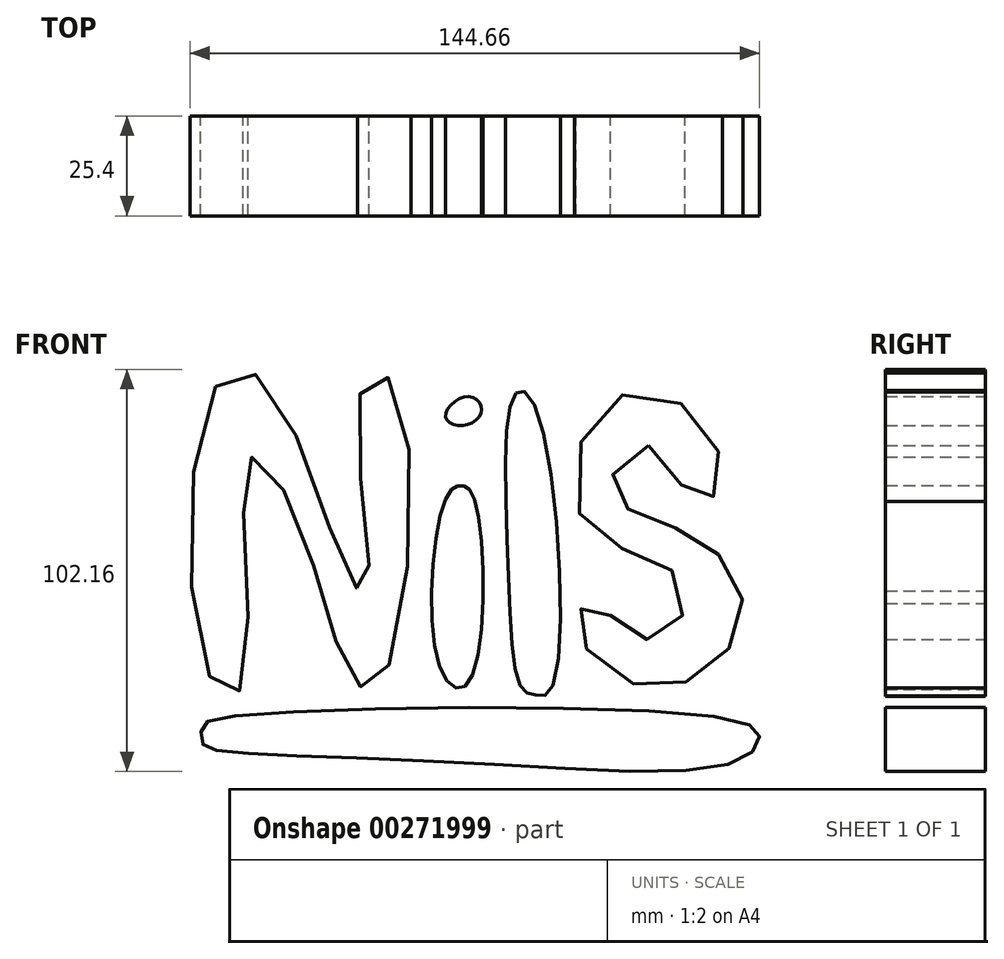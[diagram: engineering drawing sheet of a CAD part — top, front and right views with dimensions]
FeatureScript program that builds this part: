
annotation { "Feature Type Name" : "Feature", "Feature Type Description" : "" }
export const myFeature = defineFeature(function(context is Context, id is Id, definition is map)
    precondition{}
    {
        {
            var Q0;
            Q0=qCreatedBy(makeId("Front.planeOp"),FACE);
            var sketch = newSketch(context, id + "F0", { "sketchPlane" : qUnion([Q0])});
            skFitSpline(sketch, "E0", {"points": [v(-71.07, 25.18) * mm, v(-71.77, -50.12) * mm, v(-64.48, -51.3) * mm, v(-62.83, 6.35) * mm, v(-50.83, -7.3) * mm, v(-36, -49.42) * mm, v(-29.18, -49.89) * mm, v(-25.65, 25.41) * mm, v(-33.65, 25.65) * mm, v(-32.47, -25.18) * mm, v(-35.3, -26.12) * mm, v(-57.42, 24.94) * mm, v(-71.07, 25.18) * mm]});
            skFitSpline(sketch, "E1", {"points": [v(-70.8, -67.3) * mm, v(-9.62, -70.36) * mm, v(61.45, -70.13) * mm, v(67.1, -64) * mm, v(57.92, -59.07) * mm, v(-68.45, -58.83) * mm, v(-74.57, -61.65) * mm, v(-74.57, -65.42) * mm, v(-70.8, -67.3) * mm]});
            skSolve(sketch);
        }
        {
            var Q0;
            Q0=makeQuery(id+"F0.imprint","IMPRINT",FACE,{"disambiguationData":[TD([[makeQuery(id+"F0.imprint","IMPRINT",EDGE,{"derivedFrom":sQuery(id+"F0.wireOp",EDGE,"E0")}),1.0]])]});
            extrude(context, id + "F1", {"entities" : qUnion([Q0]), "depth" : 25.4 * mm});
        }
        {
            var Q0;
            Q0=qCreatedBy(makeId("Front.planeOp"),FACE);
            var sketch = newSketch(context, id + "F2", { "sketchPlane" : qUnion([Q0])});
            skFitSpline(sketch, "E2", {"points": [v(-12.68, -3.53) * mm, v(-13.62, -47.54) * mm, v(-7.03, -50.36) * mm, v(-5.15, -4) * mm, v(-8.68, 0) * mm, v(-12.68, -3.53) * mm]});
            skFitSpline(sketch, "E3", {"points": [v(-12.68, 17.41) * mm, v(-7.5, 15.3) * mm, v(-3.5, 19.53) * mm, v(-7.5, 22.6) * mm, v(-12.68, 17.41) * mm]});
            skFitSpline(sketch, "E4", {"points": [v(5.2, 23.53) * mm, v(3.08, -17.88) * mm, v(6.85, -51.77) * mm, v(10.14, -53.18) * mm, v(14.15, -52) * mm, v(10.38, 19.53) * mm, v(5.2, 23.53) * mm]});
            skFitSpline(sketch, "E5", {"points": [v(38.85, 10.12) * mm, v(50.62, -3.53) * mm, v(57.2, 0) * mm, v(48.97, 19.53) * mm, v(26.62, 19.53) * mm, v(23.32, -10.82) * mm, v(43.33, -20.24) * mm, v(47.1, -34.12) * mm, v(35.32, -38.6) * mm, v(25.68, -30.12) * mm, v(20.5, -34.12) * mm, v(32.5, -49.42) * mm, v(51.8, -48.24) * mm, v(62.86, -32.47) * mm, v(55.33, -16.24) * mm, v(38.62, -8.24) * mm, v(29.2, 0) * mm, v(38.85, 10.12) * mm]});
            skSolve(sketch);
        }
        {
            var Q0;
            Q0=makeQuery(id+"F2.imprint","IMPRINT",FACE,{"disambiguationData":[TD([[makeQuery(id+"F2.imprint","IMPRINT",EDGE,{"derivedFrom":sQuery(id+"F2.wireOp",EDGE,"E2")}),1.0]])]});
            var Q1;
            Q1=makeQuery(id+"F2.imprint","IMPRINT",FACE,{"disambiguationData":[TD([[makeQuery(id+"F2.imprint","IMPRINT",EDGE,{"derivedFrom":sQuery(id+"F2.wireOp",EDGE,"E3")}),1.0]])]});
            var Q2;
            Q2=makeQuery(id+"F2.imprint","IMPRINT",FACE,{"disambiguationData":[TD([[makeQuery(id+"F2.imprint","IMPRINT",EDGE,{"derivedFrom":sQuery(id+"F2.wireOp",EDGE,"E4")}),1.0]])]});
            var Q3;
            Q3=makeQuery(id+"F2.imprint","IMPRINT",FACE,{"disambiguationData":[TD([[makeQuery(id+"F2.imprint","IMPRINT",EDGE,{"derivedFrom":sQuery(id+"F2.wireOp",EDGE,"E5")}),1.0]])]});
            extrude(context, id + "F3", {"entities" : qUnion([Q0, Q1, Q2, Q3]), "depth" : 25.4 * mm});
        }
        {
            var Q0;
            Q0=makeQuery(id+"F0.imprint","IMPRINT",FACE,{"disambiguationData":[TD([[makeQuery(id+"F0.imprint","IMPRINT",EDGE,{"derivedFrom":sQuery(id+"F0.wireOp",EDGE,"E1")}),1.0]])]});
            extrude(context, id + "F4", {"entities" : qUnion([Q0]), "depth" : 25.4 * mm});
        }
    });
